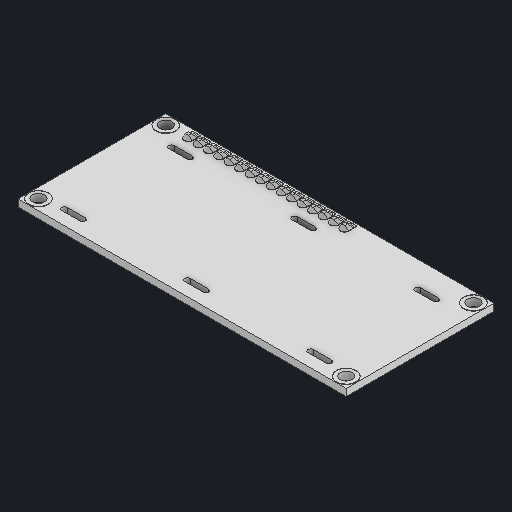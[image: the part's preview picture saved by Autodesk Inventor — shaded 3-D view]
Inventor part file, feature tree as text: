
AUTODESK INVENTOR PART (.ipt)
format: ipt  version: 2023 (Build 270158000, 158)  size: 723,456 bytes
history: native  units: in
note: dims shown in document units (in); Inventor stores cm internally (conversion verified against a paired STEP export)
features: fillet x1
ambient origin geometry x8: Origin, YZ Plane, XZ Plane, XY Plane, X Axis, Y Axis, Z Axis, Center Point
bodies: Solid1 (feature_tree)
feature tree (1):
  fillet  "Fillet6"  [1 undecoded]
note: 1 required parameter value undecoded (feature->parameter linkage not recoverable at this tier; creation-order binding heuristic only, values carry confidence <= 0.55)
